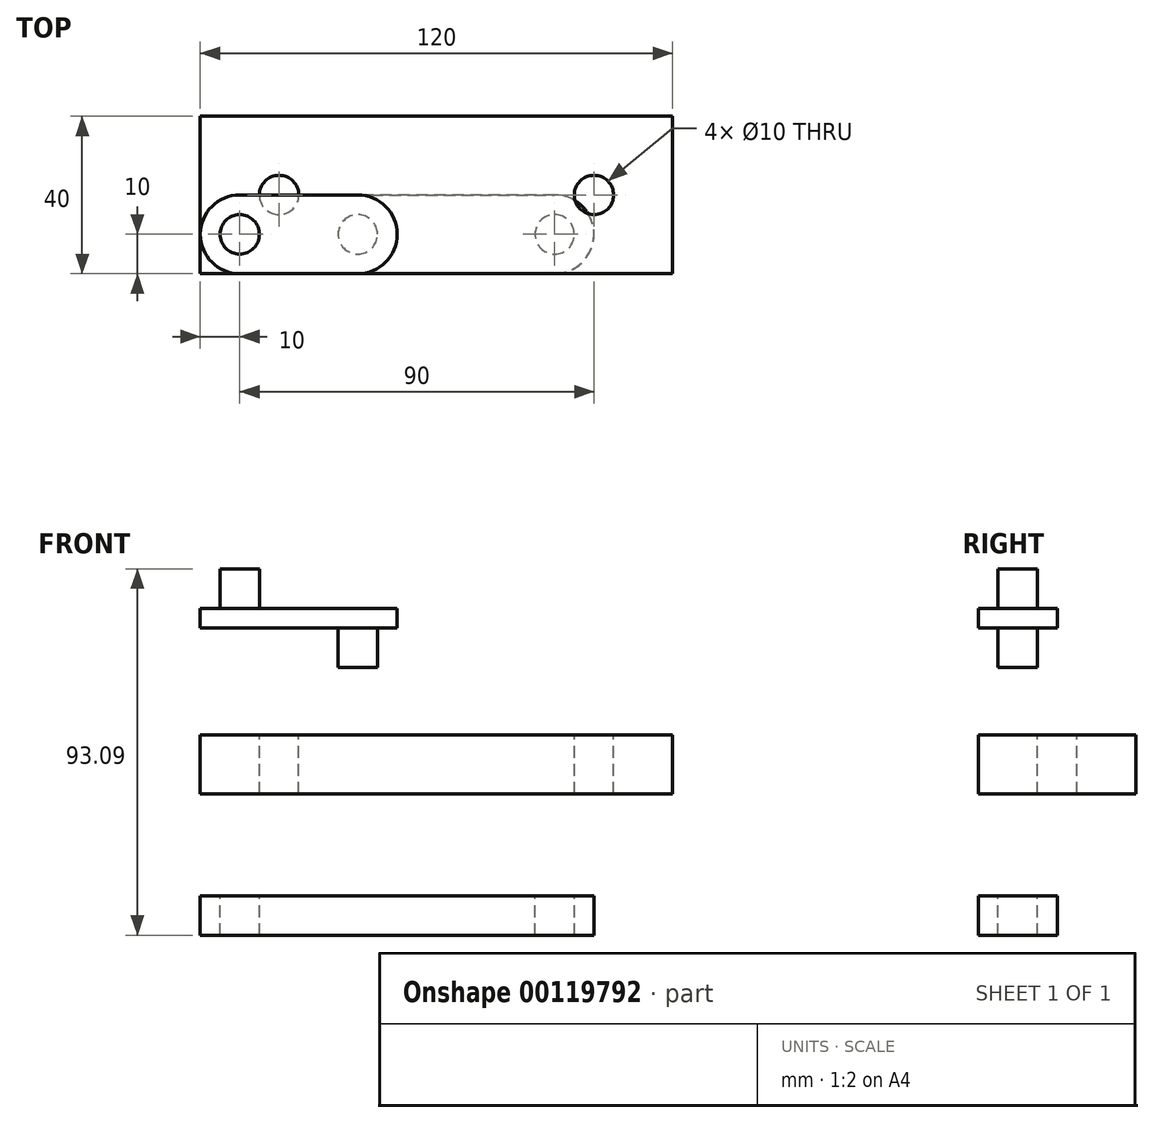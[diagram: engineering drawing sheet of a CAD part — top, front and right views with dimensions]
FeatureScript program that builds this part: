
annotation { "Feature Type Name" : "Feature", "Feature Type Description" : "" }
export const myFeature = defineFeature(function(context is Context, id is Id, definition is map)
    precondition{}
    {
        {
            var Q0;
            Q0=qCreatedBy(makeId("Front.planeOp"),FACE);
            var sketch = newSketch(context, id + "F0", { "sketchPlane" : qUnion([Q0])});
            skLineSegment(sketch, "E0", {"start": v(0, 0) * mm, "end": v(120, 0) * mm});
            skLineSegment(sketch, "E1", {"start": v(120, 0) * mm, "end": v(120, 15) * mm});
            skLineSegment(sketch, "E2", {"start": v(120, 15) * mm, "end": v(0, 15) * mm});
            skLineSegment(sketch, "E3", {"start": v(0, 15) * mm, "end": v(0, 0) * mm});
            skSolve(sketch);
        }
        {
            var Q0;
            Q0=makeQuery(id+"F0.imprint","IMPRINT",FACE,{"disambiguationData":[TD([[makeQuery(id+"F0.imprint","IMPRINT",EDGE,{"derivedFrom":sQuery(id+"F0.wireOp",EDGE,"E0")}),1.0]])]});
            extrude(context, id + "F1", {"entities" : qUnion([Q0]), "oppositeDirection" : true, "depth" : 40 * mm});
        }
        {
            var Q0;
            Q0=makeQuery(id+"F1.opExtrude","SWEPT_FACE",FACE,{"disambiguationData":[OSD([sQuery(id+"F0.wireOp",EDGE,"E2")])]});
            var sketch = newSketch(context, id + "F2", { "sketchPlane" : qUnion([Q0])});
            skLineSegment(sketch, "E4", {"start": v(0, 20) * mm, "end": v(20, 20) * mm, "construction": true});
            skLineSegment(sketch, "E5", {"start": v(120, 20) * mm, "end": v(100, 20) * mm, "construction": true});
            skCircle(sketch, "E6", {"center": v(20, 20) * mm, "radius": 5 * mm});
            skCircle(sketch, "E7", {"center": v(100, 20) * mm, "radius": 5 * mm});
            skSolve(sketch);
        }
        {
            var Q0;
            Q0 = qSketchRegion(id + "F2", true);
            extrude(context, id + "F3", {"entities" : qUnion([Q0]), "operationType" : NewBodyOperationType.REMOVE, "oppositeDirection" : true, "depth" : 37.52 * mm});
        }
        {
            var Q0;
            Q0=qCreatedBy(makeId("Front.planeOp"),FACE);
            var sketch = newSketch(context, id + "F4", { "sketchPlane" : qUnion([Q0])});
            skLineSegment(sketch, "E8", {"start": v(0, 42.18) * mm, "end": v(50, 42.18) * mm});
            skLineSegment(sketch, "E9", {"start": v(50, 42.18) * mm, "end": v(50, 47.18) * mm});
            skLineSegment(sketch, "E10", {"start": v(50, 47.18) * mm, "end": v(0, 47.18) * mm});
            skLineSegment(sketch, "E11", {"start": v(0, 47.18) * mm, "end": v(0, 42.18) * mm});
            skSolve(sketch);
        }
        {
            var Q0;
            Q0 = qSketchRegion(id + "F4", true);
            extrude(context, id + "F5", {"entities" : qUnion([Q0]), "oppositeDirection" : true, "depth" : 20 * mm});
        }
        {
            var Q0;
            Q0=makeQuery(id+"F5.opExtrude","SWEPT_FACE",FACE,{"disambiguationData":[OSD([sQuery(id+"F4.wireOp",EDGE,"E10")])]});
            var sketch = newSketch(context, id + "F6", { "sketchPlane" : qUnion([Q0])});
            skLineSegment(sketch, "E12", {"start": v(0, 10) * mm, "end": v(10, 10) * mm});
            skCircle(sketch, "E13", {"center": v(10, 10) * mm, "radius": 5 * mm});
            skSolve(sketch);
        }
        {
            var Q0;
            Q0=makeQuery(id+"F5.opExtrude","SWEPT_FACE",FACE,{"disambiguationData":[OSD([sQuery(id+"F4.wireOp",EDGE,"E8")])]});
            var sketch = newSketch(context, id + "F7", { "sketchPlane" : qUnion([Q0])});
            skLineSegment(sketch, "E14", {"start": v(50, -10) * mm, "end": v(40, -10) * mm, "construction": true});
            skCircle(sketch, "E15", {"center": v(40, -10) * mm, "radius": 5 * mm});
            skSolve(sketch);
        }
        {
            var Q0;
            Q0=makeQuery(id+"F6.imprint","IMPRINT",FACE,{"disambiguationData":[TD([[makeQuery(id+"F6.imprint","IMPRINT",EDGE,{"derivedFrom":sQuery(id+"F6.wireOp",EDGE,"E13")}),1.0]])]});
            extrude(context, id + "F8", {"entities" : qUnion([Q0]), "operationType" : NewBodyOperationType.ADD, "depth" : 10 * mm});
        }
        {
            var Q0;
            Q0=makeQuery(id+"F7.imprint","IMPRINT",FACE,{"disambiguationData":[TD([[makeQuery(id+"F7.imprint","IMPRINT",EDGE,{"derivedFrom":sQuery(id+"F7.wireOp",EDGE,"E15")}),1.0]])]});
            extrude(context, id + "F9", {"entities" : qUnion([Q0]), "operationType" : NewBodyOperationType.ADD, "depth" : 10 * mm});
        }
        {
            var Q0;
            Q0=makeQuery(id+"F5.opExtrude","CAP_EDGE",EDGE,{"disambiguationData":[OSD([sQuery(id+"F4.wireOp",EDGE,"E11")])],"isStart":false});
            var Q1;
            Q1=makeQuery(id+"F5.opExtrude","CAP_EDGE",EDGE,{"disambiguationData":[OSD([sQuery(id+"F4.wireOp",EDGE,"E11")])],"isStart":true});
            var Q2;
            Q2=makeQuery(id+"F5.opExtrude","CAP_EDGE",EDGE,{"disambiguationData":[OSD([sQuery(id+"F4.wireOp",EDGE,"E9")])],"isStart":true});
            var Q3;
            Q3=makeQuery(id+"F5.opExtrude","CAP_EDGE",EDGE,{"disambiguationData":[OSD([sQuery(id+"F4.wireOp",EDGE,"E9")])],"isStart":false});
            fillet(context, id + "F10", {"entities" : qUnion([Q0, Q1, Q2, Q3]), "radius" : 10 * mm, "tangentPropagation" : true, "allowEdgeOverflow" : false});
        }
        {
            var Q0;
            Q0=qCreatedBy(makeId("Front.planeOp"),FACE);
            var sketch = newSketch(context, id + "F11", { "sketchPlane" : qUnion([Q0])});
            skLineSegment(sketch, "E16", {"start": v(0, -25.91) * mm, "end": v(100, -25.91) * mm});
            skLineSegment(sketch, "E17", {"start": v(100, -25.91) * mm, "end": v(100, -35.91) * mm});
            skLineSegment(sketch, "E18", {"start": v(100, -35.91) * mm, "end": v(0, -35.91) * mm});
            skLineSegment(sketch, "E19", {"start": v(0, -35.91) * mm, "end": v(0, -25.91) * mm});
            skSolve(sketch);
        }
        {
            var Q0;
            Q0 = qSketchRegion(id + "F11", true);
            var Q1;
            Q1=makeQuery(id+"F11.imprint","IMPRINT",FACE,{"disambiguationData":[TD([[makeQuery(id+"F11.imprint","IMPRINT",EDGE,{"derivedFrom":sQuery(id+"F11.wireOp",EDGE,"E16")}),-1.0]])]});
            extrude(context, id + "F12", {"entities" : qUnion([Q0, Q1]), "oppositeDirection" : true, "depth" : 20 * mm});
        }
        {
            var Q0;
            Q0=makeQuery(id+"F12.opExtrude","SWEPT_FACE",FACE,{"disambiguationData":[OSD([sQuery(id+"F11.wireOp",EDGE,"E16")])]});
            var sketch = newSketch(context, id + "F13", { "sketchPlane" : qUnion([Q0])});
            skLineSegment(sketch, "E20", {"start": v(0, 10) * mm, "end": v(10, 10) * mm});
            skLineSegment(sketch, "E21", {"start": v(100, 10) * mm, "end": v(90, 10) * mm});
            skCircle(sketch, "E22", {"center": v(10, 10) * mm, "radius": 5 * mm});
            skCircle(sketch, "E23", {"center": v(90, 10) * mm, "radius": 5 * mm});
            skSolve(sketch);
        }
        {
            var Q0;
            Q0 = qSketchRegion(id + "F13", true);
            extrude(context, id + "F14", {"entities" : qUnion([Q0]), "operationType" : NewBodyOperationType.REMOVE, "oppositeDirection" : true, "depth" : 25 * mm});
        }
        {
            var Q0;
            Q0=makeQuery(id+"F12.opExtrude","CAP_EDGE",EDGE,{"disambiguationData":[OSD([sQuery(id+"F11.wireOp",EDGE,"E19")])],"isStart":true});
            var Q1;
            Q1=makeQuery(id+"F12.opExtrude","CAP_EDGE",EDGE,{"disambiguationData":[OSD([sQuery(id+"F11.wireOp",EDGE,"E19")])],"isStart":false});
            var Q2;
            Q2=makeQuery(id+"F12.opExtrude","CAP_EDGE",EDGE,{"disambiguationData":[OSD([sQuery(id+"F11.wireOp",EDGE,"E17")])],"isStart":false});
            var Q3;
            Q3=makeQuery(id+"F12.opExtrude","CAP_EDGE",EDGE,{"disambiguationData":[OSD([sQuery(id+"F11.wireOp",EDGE,"E17")])],"isStart":true});
            fillet(context, id + "F15", {"entities" : qUnion([Q0, Q1, Q2, Q3]), "radius" : 10 * mm, "tangentPropagation" : true, "allowEdgeOverflow" : false});
        }
    });
